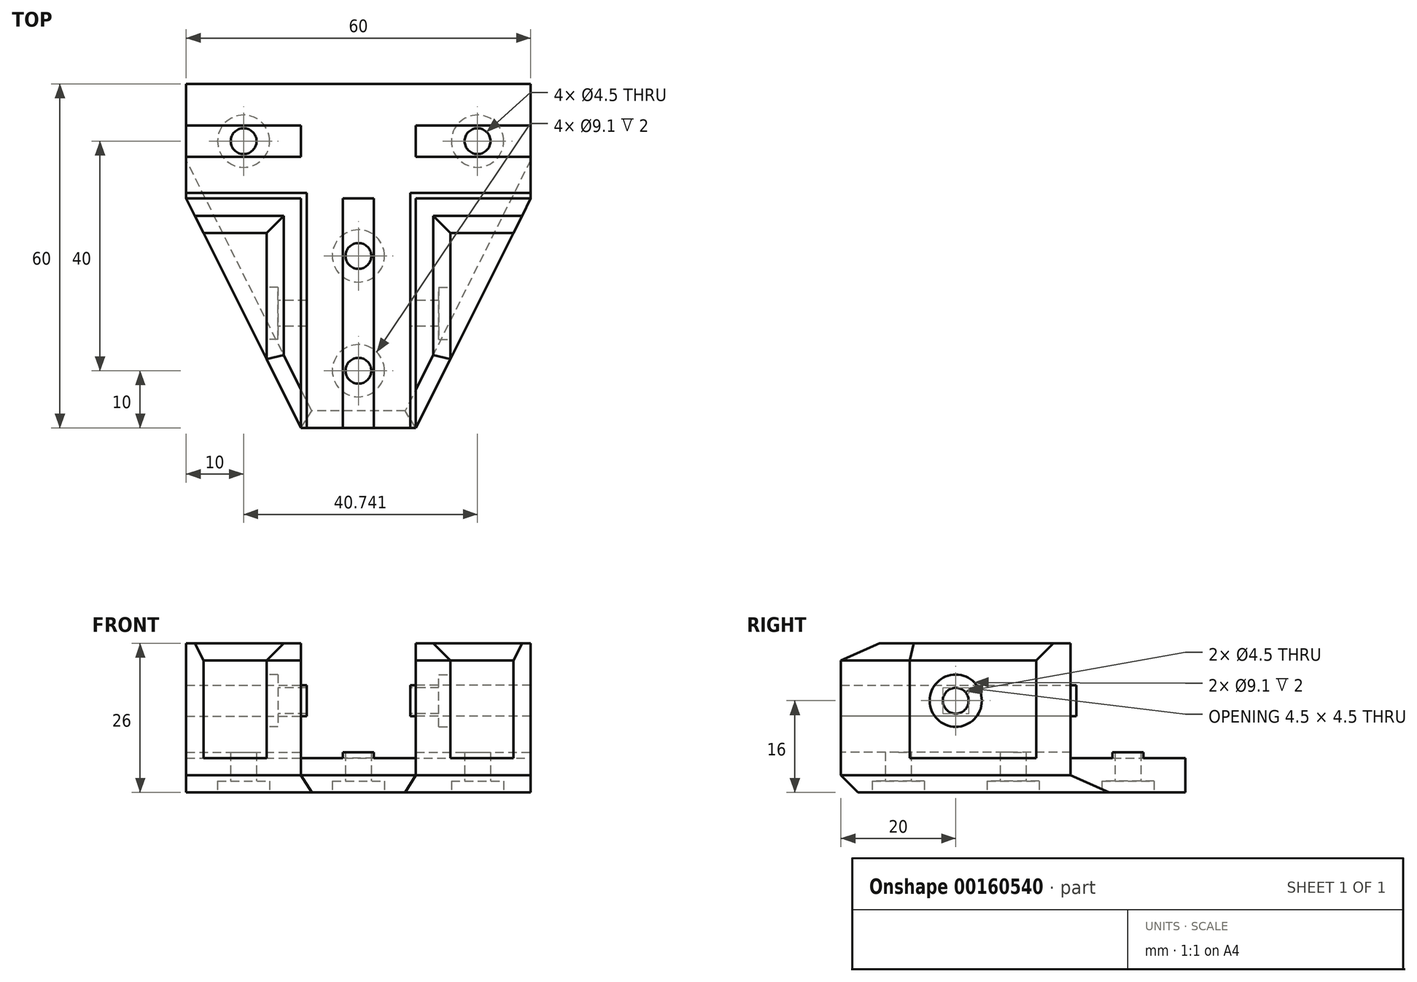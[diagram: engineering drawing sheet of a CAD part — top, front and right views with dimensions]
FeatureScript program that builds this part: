
annotation { "Feature Type Name" : "Feature", "Feature Type Description" : "" }
export const myFeature = defineFeature(function(context is Context, id is Id, definition is map)
    precondition{}
    {
        {
            var Q0;
            Q0=qCreatedBy(makeId("Top.planeOp"),FACE);
            var sketch = newSketch(context, id + "F0", { "sketchPlane" : qUnion([Q0])});
            skLineSegment(sketch, "E0", {"start": v(0, 0) * mm, "end": v(0, 20) * mm, "construction": true});
            skLineSegment(sketch, "E1", {"start": v(0, 0) * mm, "end": v(0, -40) * mm, "construction": true});
            skLineSegment(sketch, "E2", {"start": v(-10, 0) * mm, "end": v(-30, 0) * mm});
            skLineSegment(sketch, "E3", {"start": v(0, 20) * mm, "end": v(-30, 20) * mm});
            skLineSegment(sketch, "E4", {"start": v(-30, 20) * mm, "end": v(-30, 0) * mm});
            skLineSegment(sketch, "E5", {"start": v(0, 20) * mm, "end": v(30, 20) * mm});
            skLineSegment(sketch, "E6", {"start": v(30, 20) * mm, "end": v(30, 0) * mm});
            skLineSegment(sketch, "E7", {"start": v(30, 0) * mm, "end": v(10, 0) * mm});
            skLineSegment(sketch, "E8", {"start": v(0, -40) * mm, "end": v(10, -40) * mm});
            skLineSegment(sketch, "E9", {"start": v(10, -40) * mm, "end": v(10, 0) * mm});
            skLineSegment(sketch, "E10", {"start": v(0, -40) * mm, "end": v(-10, -40) * mm});
            skLineSegment(sketch, "E11", {"start": v(-10, -40) * mm, "end": v(-10, 0) * mm});
            skSolve(sketch);
        }
        {
            var Q0;
            Q0=qSketchRegion(id+"F0",true);
            extrude(context, id + "F1", {"entities" : qUnion([Q0]), "depth" : 6 * mm});
        }
        {
            var Q0;
            Q0=makeQuery(id+"F1.opExtrude","CAP_FACE",FACE,{"disambiguationData":[OSD([sQuery(id+"F0.wireOp",EDGE,"E2"),sQuery(id+"F0.wireOp",EDGE,"E3"),sQuery(id+"F0.wireOp",EDGE,"E4"),sQuery(id+"F0.wireOp",EDGE,"E5"),sQuery(id+"F0.wireOp",EDGE,"E6"),sQuery(id+"F0.wireOp",EDGE,"E7"),sQuery(id+"F0.wireOp",EDGE,"E8"),sQuery(id+"F0.wireOp",EDGE,"E9"),sQuery(id+"F0.wireOp",EDGE,"E10"),sQuery(id+"F0.wireOp",EDGE,"E11")])],"isStart":false});
            var sketch = newSketch(context, id + "F2", { "sketchPlane" : qUnion([Q0])});
            skLineSegment(sketch, "E12", {"start": v(-30, 10) * mm, "end": v(30, 10) * mm, "construction": true});
            skLineSegment(sketch, "E13", {"start": v(0, -40) * mm, "end": v(0, 0) * mm, "construction": true});
            skLineSegment(sketch, "E14", {"start": v(0, 0) * mm, "end": v(-2.71, 0) * mm});
            skLineSegment(sketch, "E15", {"start": v(-2.71, 0) * mm, "end": v(-2.7, -40) * mm});
            skLineSegment(sketch, "E16", {"start": v(2.71, -40) * mm, "end": v(2.71, 0) * mm});
            skLineSegment(sketch, "E17", {"start": v(2.71, 0) * mm, "end": v(0, 0) * mm});
            skLineSegment(sketch, "E18", {"start": v(-2.7, -40) * mm, "end": v(2.71, -40) * mm});
            skLineSegment(sketch, "E19", {"start": v(10, 10) * mm, "end": v(10, 12.7) * mm});
            skLineSegment(sketch, "E20", {"start": v(10, 12.71) * mm, "end": v(30, 12.71) * mm});
            skLineSegment(sketch, "E21", {"start": v(30, 12.71) * mm, "end": v(30, 7.3) * mm});
            skLineSegment(sketch, "E22", {"start": v(30, 7.3) * mm, "end": v(10, 7.29) * mm});
            skLineSegment(sketch, "E23", {"start": v(10, 7.29) * mm, "end": v(10, 10) * mm});
            skLineSegment(sketch, "E24", {"start": v(-30, 12.71) * mm, "end": v(-30, 7.29) * mm});
            skLineSegment(sketch, "E25", {"start": v(-30, 7.29) * mm, "end": v(-10, 7.3) * mm});
            skLineSegment(sketch, "E26", {"start": v(-10, 7.29) * mm, "end": v(-10, 12.71) * mm});
            skLineSegment(sketch, "E27", {"start": v(-10, 12.71) * mm, "end": v(-30, 12.71) * mm});
            skSolve(sketch);
        }
        {
            var Q0;
            Q0=qSketchRegion(id+"F2",true);
            extrude(context, id + "F3", {"entities" : qUnion([Q0]), "operationType" : NewBodyOperationType.ADD, "flatOperationType" : FlatOperationType.REMOVE, "offsetDistance" : 25 * mm, "depth" : 1 * mm, "domain" : OperationDomain.MODEL});
        }
        {
            var Q0;
            Q0=makeQuery(id+"F1.opExtrude","CAP_FACE",FACE,{"disambiguationData":[OSD([sQuery(id+"F0.wireOp",EDGE,"E2"),sQuery(id+"F0.wireOp",EDGE,"E3"),sQuery(id+"F0.wireOp",EDGE,"E4"),sQuery(id+"F0.wireOp",EDGE,"E5"),sQuery(id+"F0.wireOp",EDGE,"E6"),sQuery(id+"F0.wireOp",EDGE,"E7"),sQuery(id+"F0.wireOp",EDGE,"E8"),sQuery(id+"F0.wireOp",EDGE,"E9"),sQuery(id+"F0.wireOp",EDGE,"E10"),sQuery(id+"F0.wireOp",EDGE,"E11")])],"isStart":true});
            var sketch = newSketch(context, id + "F4", { "sketchPlane" : qUnion([Q0])});
            skCircle(sketch, "E28", {"center": v(-20, -10) * mm, "radius": 2.25 * mm});
            skCircle(sketch, "E29", {"center": v(0, 10) * mm, "radius": 2.25 * mm});
            skCircle(sketch, "E30", {"center": v(0, 30) * mm, "radius": 2.25 * mm});
            skCircle(sketch, "E31", {"center": v(20.74, -10) * mm, "radius": 2.25 * mm});
            skSolve(sketch);
        }
        {
            var Q0;
            Q0=qSketchRegion(id+"F4",true);
            extrude(context, id + "F5", {"entities" : qUnion([Q0]), "operationType" : NewBodyOperationType.REMOVE, "endBound" : BoundingType.THROUGH_ALL, "oppositeDirection" : true, "depth" : 25 * mm});
        }
        {
            var Q0;
            Q0=makeQuery(id+"F1.opExtrude","CAP_FACE",FACE,{"disambiguationData":[OSD([sQuery(id+"F0.wireOp",EDGE,"E2"),sQuery(id+"F0.wireOp",EDGE,"E3"),sQuery(id+"F0.wireOp",EDGE,"E4"),sQuery(id+"F0.wireOp",EDGE,"E5"),sQuery(id+"F0.wireOp",EDGE,"E6"),sQuery(id+"F0.wireOp",EDGE,"E7"),sQuery(id+"F0.wireOp",EDGE,"E8"),sQuery(id+"F0.wireOp",EDGE,"E9"),sQuery(id+"F0.wireOp",EDGE,"E10"),sQuery(id+"F0.wireOp",EDGE,"E11")])],"isStart":true});
            var sketch = newSketch(context, id + "F6", { "sketchPlane" : qUnion([Q0])});
            skCircle(sketch, "E32", {"center": v(0, 30) * mm, "radius": 4.55 * mm});
            skCircle(sketch, "E33", {"center": v(0, 10) * mm, "radius": 4.55 * mm});
            skCircle(sketch, "E34", {"center": v(20.74, -10) * mm, "radius": 4.55 * mm});
            skCircle(sketch, "E35", {"center": v(-20, -10) * mm, "radius": 4.55 * mm});
            skSolve(sketch);
        }
        {
            var Q0;
            Q0=qSketchRegion(id+"F6",true);
            extrude(context, id + "F7", {"entities" : qUnion([Q0]), "operationType" : NewBodyOperationType.REMOVE, "oppositeDirection" : true, "depth" : 2 * mm});
        }
        {
            var Q0;
            Q0=makeQuery(id+"F1.opExtrude","CAP_FACE",FACE,{"disambiguationData":[OSD([sQuery(id+"F0.wireOp",EDGE,"E2"),sQuery(id+"F0.wireOp",EDGE,"E3"),sQuery(id+"F0.wireOp",EDGE,"E4"),sQuery(id+"F0.wireOp",EDGE,"E5"),sQuery(id+"F0.wireOp",EDGE,"E6"),sQuery(id+"F0.wireOp",EDGE,"E7"),sQuery(id+"F0.wireOp",EDGE,"E8"),sQuery(id+"F0.wireOp",EDGE,"E9"),sQuery(id+"F0.wireOp",EDGE,"E10"),sQuery(id+"F0.wireOp",EDGE,"E11")])],"isStart":true});
            var sketch = newSketch(context, id + "F8", { "sketchPlane" : qUnion([Q0])});
            skLineSegment(sketch, "E36", {"start": v(-10, 40) * mm, "end": v(-30, 0) * mm});
            skLineSegment(sketch, "E37", {"start": v(-30, 0) * mm, "end": v(-10, 0) * mm});
            skLineSegment(sketch, "E38", {"start": v(-10, 0) * mm, "end": v(-10, 40) * mm});
            skLineSegment(sketch, "E39", {"start": v(10, 40) * mm, "end": v(10, 0) * mm});
            skLineSegment(sketch, "E40", {"start": v(10, 0) * mm, "end": v(30, 0) * mm});
            skLineSegment(sketch, "E41", {"start": v(30, 0) * mm, "end": v(10, 40) * mm});
            skSolve(sketch);
        }
        {
            var Q0;
            Q0=qSketchRegion(id+"F8",true);
            extrude(context, id + "F9", {"entities" : qUnion([Q0]), "operationType" : NewBodyOperationType.ADD, "flatOperationType" : FlatOperationType.REMOVE, "oppositeDirection" : true, "offsetDistance" : 25 * mm, "depth" : 6 * mm, "domain" : OperationDomain.MODEL});
        }
        {
            var Q0;
            Q0=makeQuery(id+"F9.boolean.opBoolean","MERGE",FACE,{"derivedFrom":[makeQuery(id+"F1.opExtrude","CAP_FACE",FACE,{"disambiguationData":[OSD([sQuery(id+"F0.wireOp",EDGE,"E2"),sQuery(id+"F0.wireOp",EDGE,"E3"),sQuery(id+"F0.wireOp",EDGE,"E4"),sQuery(id+"F0.wireOp",EDGE,"E5"),sQuery(id+"F0.wireOp",EDGE,"E6"),sQuery(id+"F0.wireOp",EDGE,"E7"),sQuery(id+"F0.wireOp",EDGE,"E8"),sQuery(id+"F0.wireOp",EDGE,"E9"),sQuery(id+"F0.wireOp",EDGE,"E10"),sQuery(id+"F0.wireOp",EDGE,"E11")])],"isStart":false}),makeQuery(id+"F9.opExtrude","CAP_FACE",FACE,{"disambiguationData":[OSD([sQuery(id+"F8.wireOp",EDGE,"E36"),sQuery(id+"F8.wireOp",EDGE,"E37"),sQuery(id+"F8.wireOp",EDGE,"E38")])],"isStart":false}),makeQuery(id+"F9.opExtrude","CAP_FACE",FACE,{"disambiguationData":[OSD([sQuery(id+"F8.wireOp",EDGE,"E39"),sQuery(id+"F8.wireOp",EDGE,"E40"),sQuery(id+"F8.wireOp",EDGE,"E41")])],"isStart":false})]});
            var sketch = newSketch(context, id + "F10", { "sketchPlane" : qUnion([Q0])});
            skLineSegment(sketch, "E42", {"start": v(0, 0) * mm, "end": v(10, 0) * mm, "construction": true});
            skPoint(sketch, "E42.endSnap0", {"position": v(0, 0) * mm});
            skLineSegment(sketch, "E43", {"start": v(0, 0) * mm, "end": v(-10, 0) * mm, "construction": true});
            skLineSegment(sketch, "E44", {"start": v(10, 0) * mm, "end": v(10, -40) * mm});
            skLineSegment(sketch, "E45", {"start": v(10, 0) * mm, "end": v(30, 0) * mm});
            skLineSegment(sketch, "E46", {"start": v(20, 0) * mm, "end": v(20, -6) * mm, "construction": true});
            skLineSegment(sketch, "E47", {"start": v(10, -20) * mm, "end": v(16, -20) * mm, "construction": true});
            skLineSegment(sketch, "E48", {"start": v(27, -6) * mm, "end": v(16, -6) * mm});
            skLineSegment(sketch, "E49", {"start": v(16, -6) * mm, "end": v(16, -28) * mm});
            skLineSegment(sketch, "E50", {"start": v(16, -28) * mm, "end": v(10, -40) * mm});
            skLineSegment(sketch, "E51", {"start": v(27, -6) * mm, "end": v(30, 0) * mm});
            skLineSegment(sketch, "E52", {"start": v(-10, 0) * mm, "end": v(-10, -40) * mm});
            skLineSegment(sketch, "E53", {"start": v(-30, 0) * mm, "end": v(-10, 0) * mm});
            skLineSegment(sketch, "E54", {"start": v(-20, 0) * mm, "end": v(-20, -6) * mm, "construction": true});
            skLineSegment(sketch, "E55", {"start": v(-10, -20) * mm, "end": v(-16, -20) * mm, "construction": true});
            skLineSegment(sketch, "E56", {"start": v(-27, -6) * mm, "end": v(-16, -6) * mm});
            skLineSegment(sketch, "E57", {"start": v(-16, -6) * mm, "end": v(-16, -28) * mm});
            skLineSegment(sketch, "E58", {"start": v(-16, -28) * mm, "end": v(-10, -40) * mm});
            skLineSegment(sketch, "E59", {"start": v(-27, -6) * mm, "end": v(-30, 0) * mm});
            skSolve(sketch);
        }
        {
            var Q0;
            Q0 = qSketchRegion(id + "F10", true);
            extrude(context, id + "F11", {"entities" : qUnion([Q0]), "operationType" : NewBodyOperationType.ADD, "depth" : 20 * mm});
        }
        {
            var Q0;
            Q0=makeQuery(id+"F11.opExtrude","SWEPT_FACE",FACE,{"disambiguationData":[OSD([sQuery(id+"F10.wireOp",EDGE,"E52")])]});
            var sketch = newSketch(context, id + "F12", { "sketchPlane" : qUnion([Q0])});
            skLineSegment(sketch, "E60", {"start": v(0, 16) * mm, "end": v(0, 18.71) * mm});
            skLineSegment(sketch, "E61", {"start": v(0, 18.71) * mm, "end": v(1, 18.71) * mm});
            skLineSegment(sketch, "E62", {"start": v(1, 18.71) * mm, "end": v(1, 13.29) * mm});
            skLineSegment(sketch, "E63", {"start": v(1, 13.29) * mm, "end": v(0, 13.29) * mm});
            skLineSegment(sketch, "E64", {"start": v(0, 13.29) * mm, "end": v(0, 16) * mm});
            skSolve(sketch);
        }
        {
            var Q0;
            Q0 = qSketchRegion(id + "F12", true);
            extrude(context, id + "F13", {"entities" : qUnion([Q0]), "operationType" : NewBodyOperationType.ADD, "oppositeDirection" : true, "depth" : 20 * mm});
        }
        {
            var Q0;
            Q0=makeQuery(id+"F13.boolean.opBoolean","MERGE",FACE,{"derivedFrom":[makeQuery(id+"F11.opExtrude","SWEPT_FACE",FACE,{"disambiguationData":[OSD([sQuery(id+"F10.wireOp",EDGE,"E52")])]}),makeQuery(id+"F13.opExtrude","CAP_FACE",FACE,{"disambiguationData":[OSD([sQuery(id+"F12.wireOp",EDGE,"E60"),sQuery(id+"F12.wireOp",EDGE,"E61"),sQuery(id+"F12.wireOp",EDGE,"E62"),sQuery(id+"F12.wireOp",EDGE,"E63"),sQuery(id+"F12.wireOp",EDGE,"E64")])],"isStart":true})]});
            var sketch = newSketch(context, id + "F14", { "sketchPlane" : qUnion([Q0])});
            skLineSegment(sketch, "E65.bottom", {"start": v(1, 18.71) * mm, "end": v(-40, 18.7) * mm});
            skLineSegment(sketch, "E65.top", {"start": v(1, 13.29) * mm, "end": v(-40, 13.29) * mm});
            skLineSegment(sketch, "E65.left", {"start": v(1, 18.71) * mm, "end": v(1, 13.3) * mm});
            skLineSegment(sketch, "E65.right", {"start": v(-40, 18.71) * mm, "end": v(-40, 13.29) * mm});
            skSolve(sketch);
        }
        {
            var Q0;
            Q0 = qSketchRegion(id + "F14", true);
            extrude(context, id + "F15", {"entities" : qUnion([Q0]), "operationType" : NewBodyOperationType.ADD, "flatOperationType" : FlatOperationType.REMOVE, "offsetDistance" : 25 * mm, "depth" : 1 * mm, "domain" : OperationDomain.MODEL});
        }
        {
            var Q0;
            Q0=makeQuery(id+"F11.opExtrude","SWEPT_FACE",FACE,{"disambiguationData":[OSD([sQuery(id+"F10.wireOp",EDGE,"E44")])]});
            var sketch = newSketch(context, id + "F16", { "sketchPlane" : qUnion([Q0])});
            skLineSegment(sketch, "E66", {"start": v(0, 16) * mm, "end": v(0, 18.71) * mm});
            skLineSegment(sketch, "E67", {"start": v(0, 18.71) * mm, "end": v(-1, 18.71) * mm});
            skLineSegment(sketch, "E68", {"start": v(-1, 18.71) * mm, "end": v(-1, 13.29) * mm});
            skLineSegment(sketch, "E69", {"start": v(-1, 13.29) * mm, "end": v(0, 13.29) * mm});
            skLineSegment(sketch, "E70", {"start": v(0, 13.29) * mm, "end": v(0, 16) * mm});
            skSolve(sketch);
        }
        {
            var Q0;
            Q0 = qSketchRegion(id + "F16", true);
            extrude(context, id + "F17", {"entities" : qUnion([Q0]), "operationType" : NewBodyOperationType.ADD, "oppositeDirection" : true, "depth" : 20 * mm});
        }
        {
            var Q0;
            Q0=makeQuery(id+"F17.boolean.opBoolean","MERGE",FACE,{"derivedFrom":[makeQuery(id+"F11.opExtrude","SWEPT_FACE",FACE,{"disambiguationData":[OSD([sQuery(id+"F10.wireOp",EDGE,"E44")])]}),makeQuery(id+"F17.opExtrude","CAP_FACE",FACE,{"disambiguationData":[OSD([sQuery(id+"F16.wireOp",EDGE,"E66"),sQuery(id+"F16.wireOp",EDGE,"E67"),sQuery(id+"F16.wireOp",EDGE,"E68"),sQuery(id+"F16.wireOp",EDGE,"E69"),sQuery(id+"F16.wireOp",EDGE,"E70")])],"isStart":true})]});
            var sketch = newSketch(context, id + "F18", { "sketchPlane" : qUnion([Q0])});
            skLineSegment(sketch, "E71.bottom", {"start": v(-1, 13.29) * mm, "end": v(40, 13.29) * mm});
            skLineSegment(sketch, "E71.top", {"start": v(-1, 18.71) * mm, "end": v(40, 18.71) * mm});
            skLineSegment(sketch, "E71.left", {"start": v(-1, 13.29) * mm, "end": v(-1, 18.71) * mm});
            skLineSegment(sketch, "E71.right", {"start": v(40, 13.29) * mm, "end": v(40, 18.71) * mm});
            skSolve(sketch);
        }
        {
            var Q0;
            Q0 = qSketchRegion(id + "F18", true);
            extrude(context, id + "F19", {"entities" : qUnion([Q0]), "operationType" : NewBodyOperationType.ADD, "flatOperationType" : FlatOperationType.REMOVE, "offsetDistance" : 25 * mm, "depth" : 1 * mm, "domain" : OperationDomain.MODEL});
        }
        {
            var Q0;
            Q0=makeQuery(id+"F11.opExtrude","SWEPT_FACE",FACE,{"disambiguationData":[OSD([sQuery(id+"F10.wireOp",EDGE,"E57")])]});
            var sketch = newSketch(context, id + "F20", { "sketchPlane" : qUnion([Q0])});
            skCircle(sketch, "E72", {"center": v(20, 16) * mm, "radius": 2.25 * mm});
            skSolve(sketch);
        }
        {
            var Q0;
            Q0 = qSketchRegion(id + "F20", true);
            extrude(context, id + "F21", {"entities" : qUnion([Q0]), "operationType" : NewBodyOperationType.REMOVE, "endBound" : BoundingType.THROUGH_ALL, "oppositeDirection" : true, "depth" : 25 * mm});
        }
        {
            var Q0;
            Q0=makeQuery(id+"F11.opExtrude","SWEPT_FACE",FACE,{"disambiguationData":[OSD([sQuery(id+"F10.wireOp",EDGE,"E49")])]});
            var sketch = newSketch(context, id + "F22", { "sketchPlane" : qUnion([Q0])});
            skCircle(sketch, "E73", {"center": v(-20, 16) * mm, "radius": 4.55 * mm});
            skSolve(sketch);
        }
        {
            var Q0;
            Q0 = qSketchRegion(id + "F22", true);
            extrude(context, id + "F23", {"entities" : qUnion([Q0]), "operationType" : NewBodyOperationType.REMOVE, "oppositeDirection" : true, "depth" : 2 * mm});
        }
        {
            var Q0;
            Q0=makeQuery(id+"F11.opExtrude","SWEPT_FACE",FACE,{"disambiguationData":[OSD([sQuery(id+"F10.wireOp",EDGE,"E57")])]});
            var sketch = newSketch(context, id + "F24", { "sketchPlane" : qUnion([Q0])});
            skCircle(sketch, "E74", {"center": v(20, 16) * mm, "radius": 4.55 * mm});
            skSolve(sketch);
        }
        {
            var Q0;
            Q0 = qSketchRegion(id + "F24", true);
            extrude(context, id + "F25", {"entities" : qUnion([Q0]), "operationType" : NewBodyOperationType.REMOVE, "oppositeDirection" : true, "depth" : 2 * mm});
        }
        {
            var Q0;
            Q0=makeQuery(id+"F9.opExtrude","CAP_EDGE",EDGE,{"disambiguationData":[OSD([sQuery(id+"F8.wireOp",EDGE,"Cu8PwI6T-FRIW-PbFS-y9Je-fk6Ws1agS2tI")])],"isStart":true});
            var Q1;
            Q1=makeQuery(id+"F11.boolean.opBoolean","MERGE",EDGE,{"derivedFrom":[makeQuery(id+"F9.opExtrude","SWEPT_EDGE",EDGE,{"disambiguationData":[OSD([sQuery(id+"F8.wireOp",EDGE,"Cu8PwI6T-FRIW-PbFS-y9Je-fk6Ws1agS2tI"),sQuery(id+"F8.wireOp",EDGE,"ZyDlOVXI-DR5k-ICq8-FapA-tYmQKara69bz")])]}),makeQuery(id+"F11.opExtrude","SWEPT_EDGE",EDGE,{"disambiguationData":[OSD([sQuery(id+"F10.wireOp",EDGE,"XcrGgQ2H-dSCI-Vu5U-8b1r-4G8MrB20rmi3.bottom"),sQuery(id+"F10.wireOp",EDGE,"XcrGgQ2H-dSCI-Vu5U-8b1r-4G8MrB20rmi3.right")])]})]});
            var Q2;
            Q2=makeQuery(id+"F11.boolean.opBoolean","MERGE",EDGE,{"derivedFrom":[makeQuery(id+"F9.opExtrude","SWEPT_EDGE",EDGE,{"disambiguationData":[OSD([sQuery(id+"F8.wireOp",EDGE,"lFTEXkPD-j82P-dM0b-Upz0-4jfQUIbIQWBJ"),sQuery(id+"F8.wireOp",EDGE,"Cu8PwI6T-FRIW-PbFS-y9Je-fk6Ws1agS2tI")])]}),makeQuery(id+"F11.opExtrude","SWEPT_EDGE",EDGE,{"disambiguationData":[OSD([sQuery(id+"F10.wireOp",EDGE,"XcrGgQ2H-dSCI-Vu5U-8b1r-4G8MrB20rmi3.bottom"),sQuery(id+"F10.wireOp",EDGE,"XcrGgQ2H-dSCI-Vu5U-8b1r-4G8MrB20rmi3.left")])]})]});
            var Q3;
            Q3=makeQuery(id+"F9.boolean.opBoolean","MERGE",EDGE,{"derivedFrom":[makeQuery(id+"F1.opExtrude","CAP_EDGE",EDGE,{"disambiguationData":[OSD([sQuery(id+"F0.wireOp",EDGE,"E4")])],"isStart":true}),makeQuery(id+"F9.opExtrude","CAP_EDGE",EDGE,{"disambiguationData":[OSD([sQuery(id+"F8.wireOp",EDGE,"lFTEXkPD-j82P-dM0b-Upz0-4jfQUIbIQWBJ")])],"isStart":true})]});
            var Q4;
            Q4=makeQuery(id+"F9.boolean.opBoolean","MERGE",EDGE,{"derivedFrom":[makeQuery(id+"F1.opExtrude","CAP_EDGE",EDGE,{"disambiguationData":[OSD([sQuery(id+"F0.wireOp",EDGE,"E6")])],"isStart":true}),makeQuery(id+"F9.opExtrude","CAP_EDGE",EDGE,{"disambiguationData":[OSD([sQuery(id+"F8.wireOp",EDGE,"ZyDlOVXI-DR5k-ICq8-FapA-tYmQKara69bz")])],"isStart":true})]});
            var Q5;
            Q5=makeQuery(id+"F9.opExtrude","CAP_EDGE",EDGE,{"disambiguationData":[OSD([sQuery(id+"F8.wireOp",EDGE,"E41")])],"isStart":true});
            var Q6;
            Q6=makeQuery(id+"F9.opExtrude","CAP_EDGE",EDGE,{"disambiguationData":[OSD([sQuery(id+"F8.wireOp",EDGE,"E36")])],"isStart":true});
            var Q7;
            Q7=makeQuery(id+"F1.opExtrude","CAP_EDGE",EDGE,{"disambiguationData":[OSD([sQuery(id+"F0.wireOp",EDGE,"E8"),sQuery(id+"F0.wireOp",EDGE,"E10")])],"isStart":true});
            var Q8;
            Q8=makeQuery(id+"F11.opExtrude","CAP_EDGE",EDGE,{"disambiguationData":[OSD([sQuery(id+"F10.wireOp",EDGE,"XcrGgQ2H-dSCI-Vu5U-8b1r-4G8MrB20rmi3.bottom")])],"isStart":false});
            var Q9;
            Q9=makeQuery(id+"F11.opExtrude","CAP_EDGE",EDGE,{"disambiguationData":[OSD([sQuery(id+"F10.wireOp",EDGE,"E56")])],"isStart":false});
            var Q10;
            Q10=makeQuery(id+"F11.opExtrude","CAP_EDGE",EDGE,{"disambiguationData":[OSD([sQuery(id+"F10.wireOp",EDGE,"E57")])],"isStart":false});
            var Q11;
            Q11=makeQuery(id+"F11.opExtrude","CAP_EDGE",EDGE,{"disambiguationData":[OSD([sQuery(id+"F10.wireOp",EDGE,"E49")])],"isStart":false});
            var Q12;
            Q12=makeQuery(id+"F11.opExtrude","CAP_EDGE",EDGE,{"disambiguationData":[OSD([sQuery(id+"F10.wireOp",EDGE,"E48")])],"isStart":false});
            var Q13;
            Q13=makeQuery(id+"F11.opExtrude","CAP_EDGE",EDGE,{"disambiguationData":[OSD([sQuery(id+"F10.wireOp",EDGE,"E58")])],"isStart":false});
            var Q14;
            Q14=makeQuery(id+"F11.opExtrude","CAP_EDGE",EDGE,{"disambiguationData":[OSD([sQuery(id+"F10.wireOp",EDGE,"E50")])],"isStart":false});
            chamfer(context, id + "F26", {"entities" : qUnion([Q0, Q1, Q2, Q3, Q4, Q5, Q6, Q7, Q8, Q9, Q10, Q11, Q12, Q13, Q14]), "width" : 3 * mm, "tangentPropagation" : true});
        }
    });
